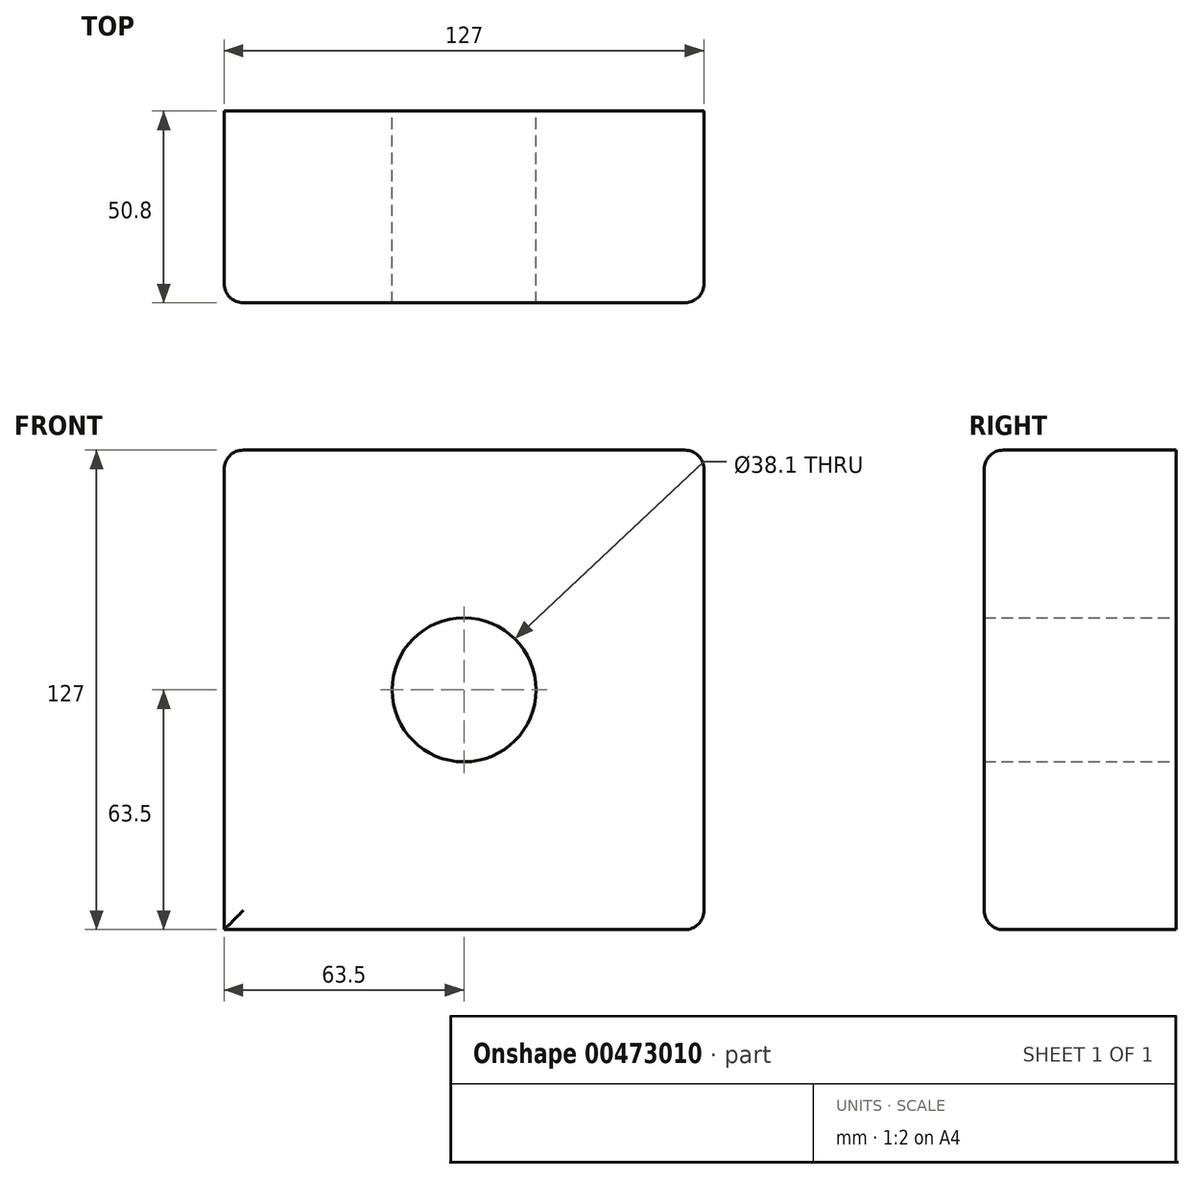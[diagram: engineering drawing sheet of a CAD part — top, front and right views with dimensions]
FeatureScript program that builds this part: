
annotation { "Feature Type Name" : "Feature", "Feature Type Description" : "" }
export const myFeature = defineFeature(function(context is Context, id is Id, definition is map)
    precondition{}
    {
        {
            var Q0;
            Q0=qCreatedBy(makeId("Front.planeOp"),FACE);
            var sketch = newSketch(context, id + "F0", { "sketchPlane" : qUnion([Q0])});
            skLineSegment(sketch, "E0.bottom", {"start": v(-63.5, 63.5) * mm, "end": v(63.5, 63.5) * mm});
            skLineSegment(sketch, "E0.top", {"start": v(-63.5, -63.5) * mm, "end": v(63.5, -63.5) * mm});
            skLineSegment(sketch, "E0.left", {"start": v(-63.5, 63.5) * mm, "end": v(-63.5, -63.5) * mm});
            skLineSegment(sketch, "E0.right", {"start": v(63.5, 63.5) * mm, "end": v(63.5, -63.5) * mm});
            skCircle(sketch, "E1", {"center": v(0, 0) * mm, "radius": 19.05 * mm});
            skSolve(sketch);
        }
        {
            var Q0;
            Q0 = qSketchRegion(id + "F0", true);
            extrude(context, id + "F1", {"entities" : qUnion([Q0]), "depth" : 50.8 * mm});
        }
        {
            var Q0;
            Q0=makeQuery(id+"F1.opExtrude","CAP_EDGE",EDGE,{"disambiguationData":[OSD([sQuery(id+"F0.wireOp",EDGE,"E0.left")])],"isStart":false});
            var Q1;
            Q1=makeQuery(id+"F1.opExtrude","CAP_EDGE",EDGE,{"disambiguationData":[OSD([sQuery(id+"F0.wireOp",EDGE,"E0.right")])],"isStart":false});
            var Q2;
            Q2=makeQuery(id+"F1.opExtrude","CAP_EDGE",EDGE,{"disambiguationData":[OSD([sQuery(id+"F0.wireOp",EDGE,"E0.top")])],"isStart":false});
            var Q3;
            Q3=makeQuery(id+"F1.opExtrude","CAP_EDGE",EDGE,{"disambiguationData":[OSD([sQuery(id+"F0.wireOp",EDGE,"E0.bottom")])],"isStart":false});
            var Q4;
            Q4=makeQuery(id+"F1.opExtrude","SWEPT_EDGE",EDGE,{"disambiguationData":[OSD([sQuery(id+"F0.wireOp",EDGE,"E0.top"),sQuery(id+"F0.wireOp",EDGE,"E0.right")])]});
            var Q5;
            Q5=makeQuery(id+"F1.opExtrude","SWEPT_EDGE",EDGE,{"disambiguationData":[OSD([sQuery(id+"F0.wireOp",EDGE,"E0.bottom"),sQuery(id+"F0.wireOp",EDGE,"E0.right")])]});
            var Q6;
            Q6=makeQuery(id+"F1.opExtrude","SWEPT_EDGE",EDGE,{"disambiguationData":[OSD([sQuery(id+"F0.wireOp",EDGE,"E0.bottom"),sQuery(id+"F0.wireOp",EDGE,"E0.left")])]});
            fillet(context, id + "F2", {"entities" : qUnion([Q0, Q1, Q2, Q3, Q4, Q5, Q6]), "radius" : 5.08 * mm, "tangentPropagation" : true, "allowEdgeOverflow" : false});
        }
    });
